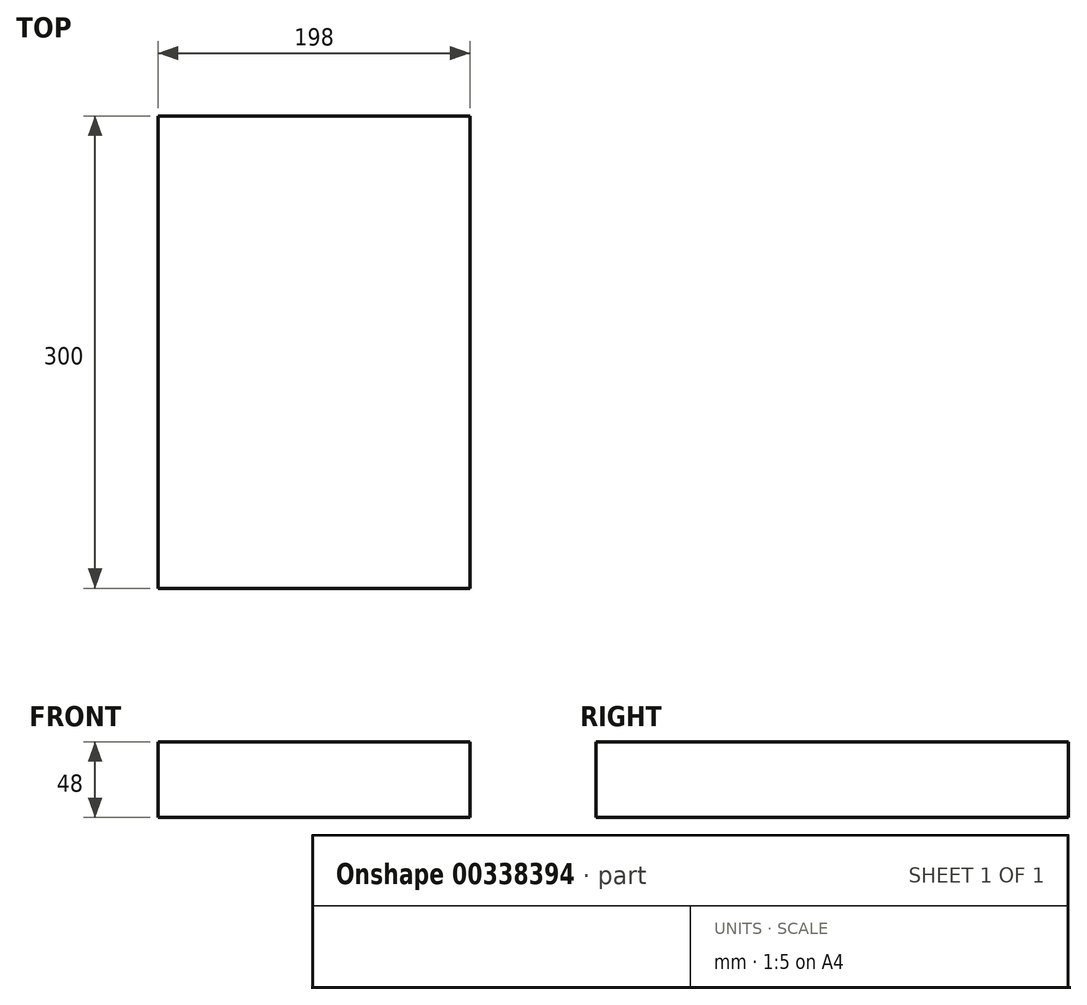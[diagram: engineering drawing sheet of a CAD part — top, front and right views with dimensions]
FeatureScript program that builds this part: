
annotation { "Feature Type Name" : "Feature", "Feature Type Description" : "" }
export const myFeature = defineFeature(function(context is Context, id is Id, definition is map)
    precondition{}
    {
        {
            var Q0;
            Q0=qCreatedBy(makeId("Front.planeOp"),FACE);
            var sketch = newSketch(context, id + "F0", { "sketchPlane" : qUnion([Q0])});
            skLineSegment(sketch, "E0.bottom", {"start": v(-99, -24) * mm, "end": v(99, -24) * mm});
            skLineSegment(sketch, "E0.top", {"start": v(-99, 24) * mm, "end": v(99, 24) * mm});
            skLineSegment(sketch, "E0.left", {"start": v(-99, -24) * mm, "end": v(-99, 24) * mm});
            skLineSegment(sketch, "E0.right", {"start": v(99, -24) * mm, "end": v(99, 24) * mm});
            skPoint(sketch, "E0.middle", {"position": v(0, 0) * mm});
            skSolve(sketch);
        }
        {
            var Q0;
            Q0=makeQuery(id+"F0.imprint","IMPRINT",FACE,{"disambiguationData":[TD([[makeQuery(id+"F0.imprint","IMPRINT",EDGE,{"derivedFrom":sQuery(id+"F0.wireOp",EDGE,"E0.bottom")}),1.0]])]});
            extrude(context, id + "F1", {"entities" : qUnion([Q0]), "depth" : 300 * mm});
        }
    });
